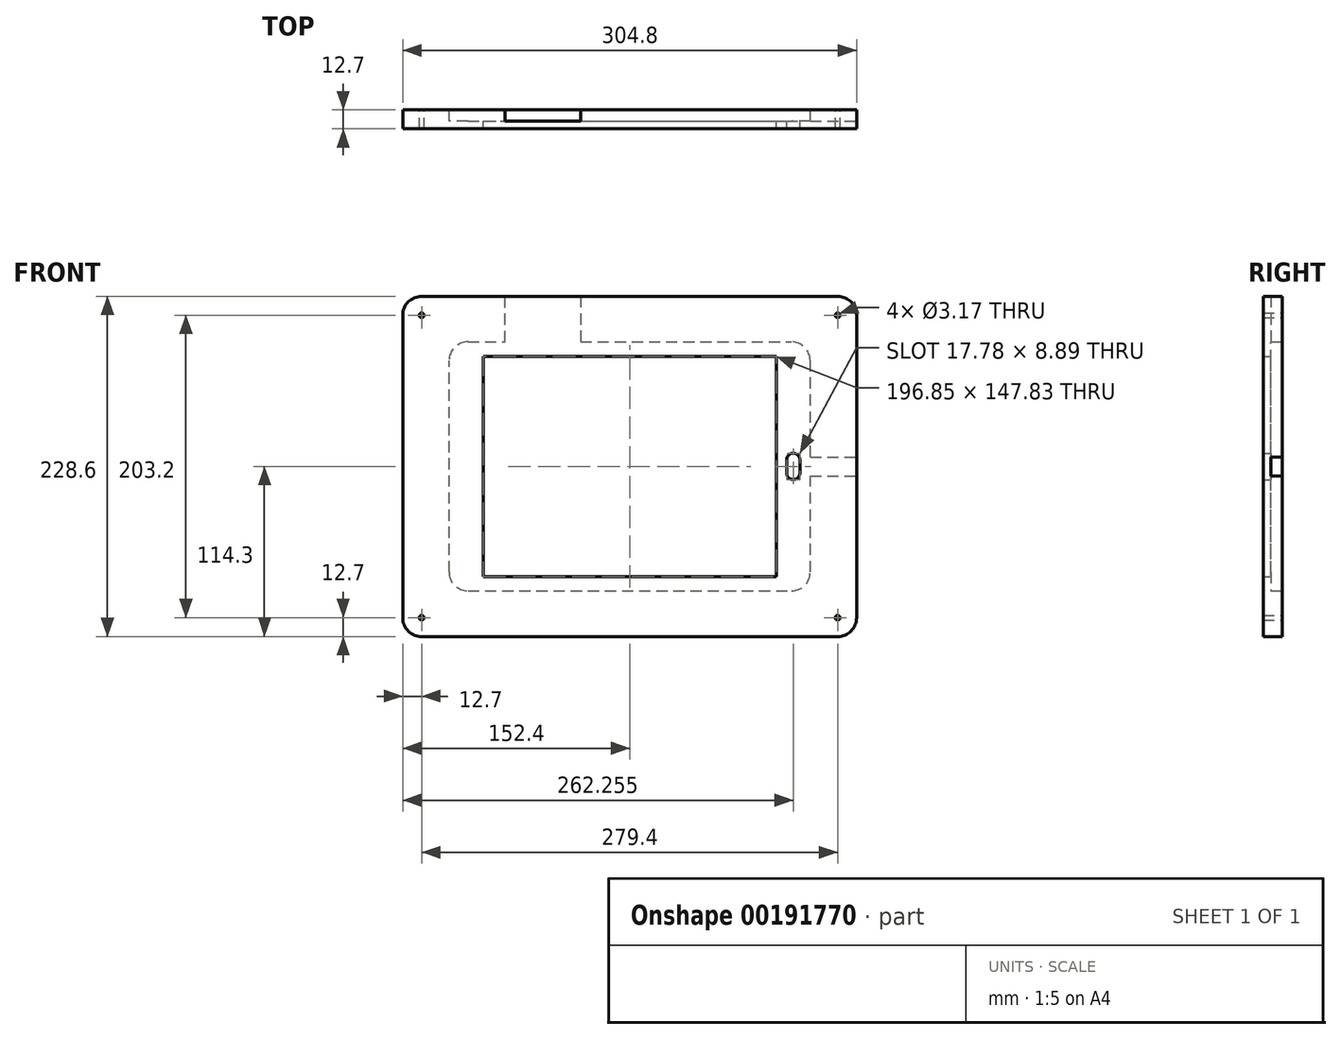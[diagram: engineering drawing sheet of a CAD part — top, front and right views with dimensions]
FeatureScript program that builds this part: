
annotation { "Feature Type Name" : "Feature", "Feature Type Description" : "" }
export const myFeature = defineFeature(function(context is Context, id is Id, definition is map)
    precondition{}
    {
        {
            var Q0;
            Q0=qCreatedBy(makeId("Front.planeOp"),FACE);
            var sketch = newSketch(context, id + "F0", { "sketchPlane" : qUnion([Q0])});
            skLineSegment(sketch, "E0.bottom", {"start": v(12.7, 228.6) * mm, "end": v(292.1, 228.6) * mm});
            skLineSegment(sketch, "E0.top", {"start": v(12.7, 0) * mm, "end": v(292.1, 0) * mm});
            skLineSegment(sketch, "E0.left", {"start": v(0, 215.9) * mm, "end": v(0, 12.7) * mm});
            skLineSegment(sketch, "E0.right", {"start": v(304.8, 215.9) * mm, "end": v(304.8, 12.7) * mm});
            skPoint(sketch, "E1.visualSharp", {"position": v(0, 228.6) * mm});
            skArc(sketch, "E1.filletArc", {"start": v(12.7, 228.6) * mm, "mid": v(3.72, 224.88) * mm, "end": v(0, 215.9) * mm});
            skPoint(sketch, "E2.visualSharp", {"position": v(304.8, 228.6) * mm});
            skArc(sketch, "E2.filletArc", {"start": v(304.8, 215.9) * mm, "mid": v(301.08, 224.88) * mm, "end": v(292.1, 228.6) * mm});
            skPoint(sketch, "E3.visualSharp", {"position": v(304.8, 0) * mm});
            skArc(sketch, "E3.filletArc", {"start": v(292.1, 0) * mm, "mid": v(301.08, 3.72) * mm, "end": v(304.8, 12.7) * mm});
            skPoint(sketch, "E4.visualSharp", {"position": v(0, 0) * mm});
            skArc(sketch, "E4.filletArc", {"start": v(0, 12.7) * mm, "mid": v(3.72, 3.72) * mm, "end": v(12.7, 0) * mm});
            skCircle(sketch, "E5", {"center": v(12.7, 215.9) * mm, "radius": 1.59 * mm});
            skCircle(sketch, "E6", {"center": v(292.1, 215.9) * mm, "radius": 1.59 * mm});
            skCircle(sketch, "E7", {"center": v(12.7, 12.7) * mm, "radius": 1.59 * mm});
            skCircle(sketch, "E8", {"center": v(292.1, 12.7) * mm, "radius": 1.59 * mm});
            skSolve(sketch);
        }
        {
            var Q0;
            Q0 = qSketchRegion(id + "F0", true);
            extrude(context, id + "F1", {"entities" : qUnion([Q0]), "depth" : 12.7 * mm});
        }
        {
            var Q0;
            Q0=makeQuery(id+"F0.imprint","IMPRINT",FACE,{"disambiguationData":[TD([[makeQuery(id+"F0.imprint","IMPRINT",EDGE,{"derivedFrom":sQuery(id+"F0.wireOp",EDGE,"E0.bottom")}),-1.0]])]});
            var sketch = newSketch(context, id + "F2", { "sketchPlane" : qUnion([Q0])});
            skLineSegment(sketch, "E9.bottom", {"start": v(43.81, 30.6) * mm, "end": v(260.99, 30.6) * mm});
            skLineSegment(sketch, "E9.top", {"start": v(43.81, 198) * mm, "end": v(68.58, 198) * mm});
            skLineSegment(sketch, "E9.left", {"start": v(31.12, 43.3) * mm, "end": v(31.11, 185.3) * mm});
            skLineSegment(sketch, "E9.right", {"start": v(273.69, 43.3) * mm, "end": v(273.69, 107.95) * mm});
            skLineSegment(sketch, "E10", {"start": v(273.69, 120.65) * mm, "end": v(304.8, 120.65) * mm});
            skLineSegment(sketch, "E11", {"start": v(273.69, 107.95) * mm, "end": v(304.8, 107.95) * mm});
            skLineSegment(sketch, "E12", {"start": v(31.11, 114.3) * mm, "end": v(304.8, 114.3) * mm, "construction": true});
            skPoint(sketch, "E13.visualSharp", {"position": v(31.11, 198) * mm});
            skArc(sketch, "E13.filletArc", {"start": v(43.81, 198) * mm, "mid": v(34.83, 194.27) * mm, "end": v(31.11, 185.3) * mm});
            skPoint(sketch, "E14.visualSharp", {"position": v(273.69, 198) * mm});
            skArc(sketch, "E14.filletArc", {"start": v(273.69, 185.3) * mm, "mid": v(269.97, 194.27) * mm, "end": v(260.99, 198) * mm});
            skPoint(sketch, "E15.visualSharp", {"position": v(31.12, 30.6) * mm});
            skArc(sketch, "E15.filletArc", {"start": v(31.11, 43.3) * mm, "mid": v(34.83, 34.33) * mm, "end": v(43.81, 30.6) * mm});
            skPoint(sketch, "E16.visualSharp", {"position": v(273.69, 30.6) * mm});
            skArc(sketch, "E16.filletArc", {"start": v(260.99, 30.6) * mm, "mid": v(269.97, 34.33) * mm, "end": v(273.69, 43.3) * mm});
            skLineSegment(sketch, "E17.trimOffspring", {"start": v(273.69, 120.65) * mm, "end": v(273.69, 185.3) * mm});
            skPoint(sketch, "E18.orphan", {"position": v(0, 114.3) * mm});
            skLineSegment(sketch, "E19", {"start": v(304.8, 120.65) * mm, "end": v(304.94, 120.65) * mm});
            skLineSegment(sketch, "E20", {"start": v(304.94, 120.65) * mm, "end": v(304.94, 107.95) * mm});
            skLineSegment(sketch, "E21", {"start": v(304.94, 107.95) * mm, "end": v(304.8, 107.95) * mm});
            skLineSegment(sketch, "E22", {"start": v(68.58, 198) * mm, "end": v(68.58, 228.64) * mm});
            skLineSegment(sketch, "E23", {"start": v(68.58, 228.64) * mm, "end": v(119.38, 228.64) * mm});
            skLineSegment(sketch, "E24", {"start": v(119.38, 228.64) * mm, "end": v(119.38, 198) * mm});
            skLineSegment(sketch, "E25.trimOffspring", {"start": v(119.38, 198) * mm, "end": v(260.99, 198) * mm});
            skSolve(sketch);
        }
        {
            var Q0;
            Q0=makeQuery(id+"F2.imprint","IMPRINT",FACE,{"disambiguationData":[TD([[makeQuery(id+"F2.imprint","IMPRINT",EDGE,{"derivedFrom":sQuery(id+"F2.wireOp",EDGE,"E9.bottom")}),1.0]])]});
            extrude(context, id + "F3", {"entities" : qUnion([Q0]), "operationType" : NewBodyOperationType.REMOVE, "depth" : 7.62 * mm});
        }
        {
            var Q0;
            Q0=makeQuery(id+"F0.imprint","IMPRINT",FACE,{"disambiguationData":[TD([[makeQuery(id+"F0.imprint","IMPRINT",EDGE,{"derivedFrom":sQuery(id+"F0.wireOp",EDGE,"E0.bottom")}),-1.0]])]});
            var sketch = newSketch(context, id + "F4", { "sketchPlane" : qUnion([Q0])});
            skLineSegment(sketch, "E26.bottom", {"start": v(250.82, 188.21) * mm, "end": v(53.97, 188.21) * mm});
            skLineSegment(sketch, "E26.top", {"start": v(250.83, 40.39) * mm, "end": v(53.98, 40.39) * mm});
            skLineSegment(sketch, "E26.left", {"start": v(250.82, 188.21) * mm, "end": v(250.83, 40.39) * mm});
            skLineSegment(sketch, "E26.right", {"start": v(53.97, 188.21) * mm, "end": v(53.98, 40.39) * mm});
            skLineSegment(sketch, "E27.bottom", {"start": v(262.25, 123.2) * mm, "end": v(262.25, 123.2) * mm});
            skLineSegment(sketch, "E27.top", {"start": v(262.25, 105.41) * mm, "end": v(262.25, 105.41) * mm});
            skLineSegment(sketch, "E27.left", {"start": v(266.7, 118.75) * mm, "end": v(266.7, 109.86) * mm});
            skLineSegment(sketch, "E27.right", {"start": v(257.8, 118.75) * mm, "end": v(257.8, 109.86) * mm});
            skPoint(sketch, "E28.visualSharp", {"position": v(266.7, 123.2) * mm});
            skArc(sketch, "E28.filletArc", {"start": v(266.7, 118.75) * mm, "mid": v(265.4, 121.89) * mm, "end": v(262.25, 123.2) * mm});
            skPoint(sketch, "E29.visualSharp", {"position": v(257.8, 123.2) * mm});
            skArc(sketch, "E29.filletArc", {"start": v(262.25, 123.2) * mm, "mid": v(259.11, 121.89) * mm, "end": v(257.8, 118.75) * mm});
            skPoint(sketch, "E30.visualSharp", {"position": v(266.7, 105.41) * mm});
            skArc(sketch, "E30.filletArc", {"start": v(262.25, 105.41) * mm, "mid": v(265.4, 106.71) * mm, "end": v(266.7, 109.86) * mm});
            skPoint(sketch, "E31.visualSharp", {"position": v(257.8, 105.41) * mm});
            skArc(sketch, "E31.filletArc", {"start": v(257.8, 109.86) * mm, "mid": v(259.11, 106.71) * mm, "end": v(262.25, 105.41) * mm});
            skCircle(sketch, "E32.0", {"center": v(292.1, 215.9) * mm, "radius": 1.59 * mm});
            skCircle(sketch, "E32.1", {"center": v(12.7, 215.9) * mm, "radius": 1.59 * mm});
            skCircle(sketch, "E32.2", {"center": v(12.7, 12.7) * mm, "radius": 1.59 * mm});
            skCircle(sketch, "E32.3", {"center": v(292.1, 12.7) * mm, "radius": 1.59 * mm});
            skSolve(sketch);
        }
        {
            var Q0;
            Q0 = qSketchRegion(id + "F4", true);
            extrude(context, id + "F5", {"entities" : qUnion([Q0]), "operationType" : NewBodyOperationType.REMOVE, "depth" : 25.4 * mm});
        }
    });
